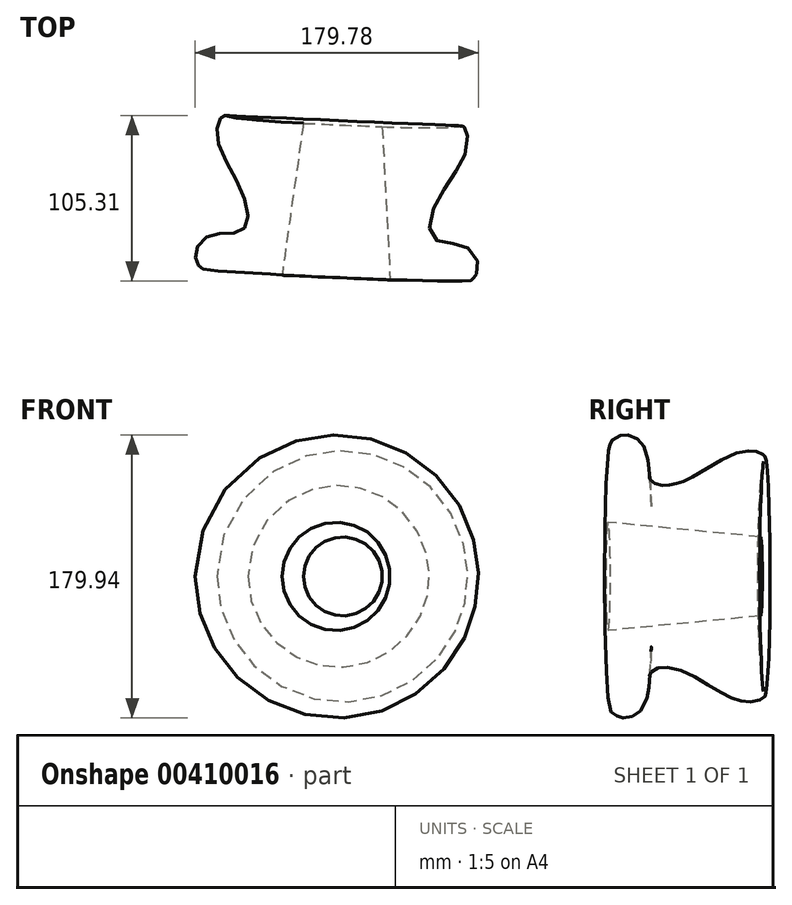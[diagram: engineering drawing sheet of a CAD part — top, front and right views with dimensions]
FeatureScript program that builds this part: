
annotation { "Feature Type Name" : "Feature", "Feature Type Description" : "" }
export const myFeature = defineFeature(function(context is Context, id is Id, definition is map)
    precondition{}
    {
        {
            var Q0;
            Q0=qCreatedBy(makeId("Top.planeOp"),FACE);
            var sketch = newSketch(context, id + "F0", { "sketchPlane" : qUnion([Q0])});
            skLineSegment(sketch, "E0", {"start": v(-58.04, 49.13) * mm, "end": v(-60.72, -11.82) * mm});
            skFitSpline(sketch, "E1", {"points": [v(-32.95, 49.13) * mm, v(14.94, 49.24) * mm, v(18.83, 49.2) * mm, v(20.84, 35.47) * mm, v(0, -1.91) * mm, v(0, -22.2) * mm, v(19.67, -26.78) * mm, v(28.1, -39.96) * mm, v(24.92, -47.26) * mm, v(19.7, -48.94) * mm, v(-27.9, -48.2) * mm, v(-27.91, -48.2) * mm], "startDerivative": vector(282.81, -11.39) * mm, "endDerivative": vector(-12.26, 11.34) * mm});
            skPoint(sketch, "E2.end.orphan", {"position": v(-27.9, -53.16) * mm});
            skLineSegment(sketch, "E3", {"start": v(-32.95, 49.13) * mm, "end": v(-27.9, -48.2) * mm});
            skSolve(sketch);
        }
        {
            var Q0;
            {var subQ0=sQuery(id+"F0.wireOp",EDGE,"E3");var subQ1=sQuery(id+"F0.wireOp",EDGE,"E1");var subQ2=makeQuery(id+"F0.imprint","INTERSECT",VERTEX,{"disambiguationData":[OD(0.0)],"derivedFrom":[subQ1,subQ0]});Q0=makeQuery(id+"F0.imprint","IMPRINT",FACE,{"disambiguationData":[TD([[makeQuery(id+"F0.imprint","IMPRINT",EDGE,{"disambiguationData":[TD([[subQ2,-1.0]])],"derivedFrom":subQ1}),-1.0]])]});}
            var Q1;
            Q1=sQuery(id+"F0.wireOp",EDGE,"E0");
            revolve(context, id + "F1", {"entities" : qUnion([Q0]), "axis" : qUnion([Q1]), "revolveType" : RevolveType.FULL});
        }
    });
